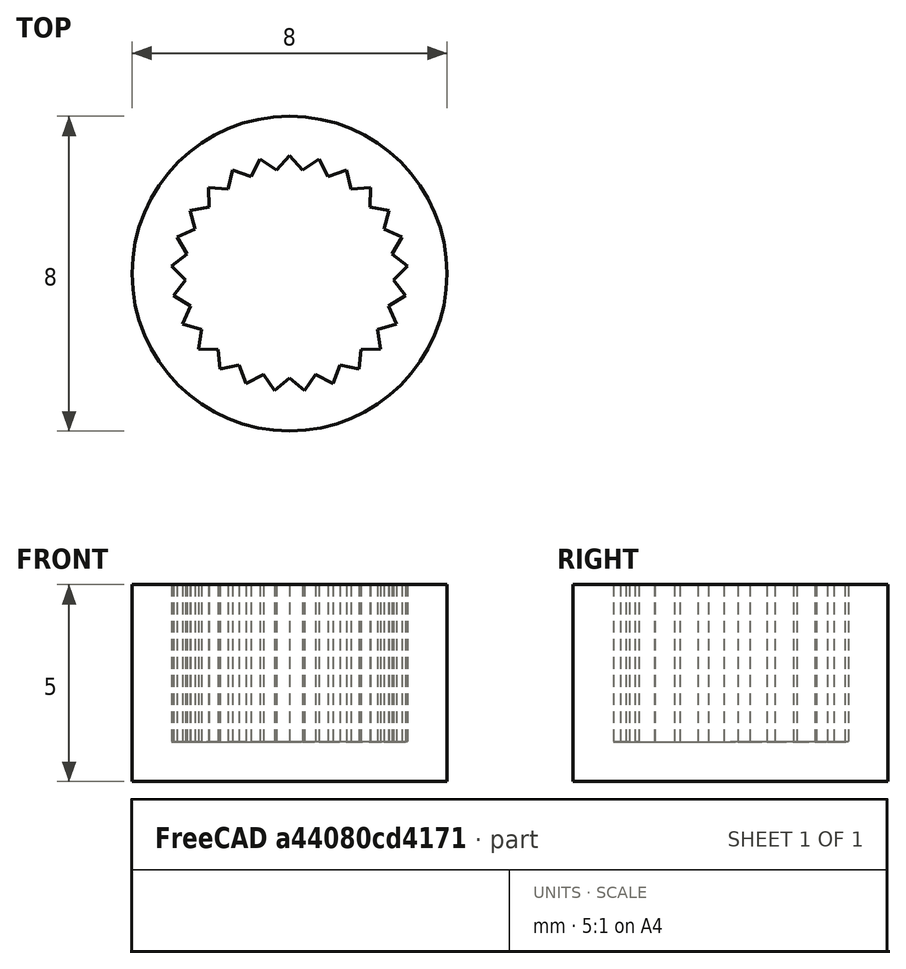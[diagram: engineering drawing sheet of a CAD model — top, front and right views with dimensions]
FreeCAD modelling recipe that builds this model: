
FCSTD DOCUMENT  (FreeCAD 0.20R29410 (Git))
Label: basic_spline
License: All rights reserved
LicenseURL: http://en.wikipedia.org/wiki/All_rights_reserved
objects: Sketcher::SketchObject×2, Mesh::Feature×1, PartDesign::Pad×1, PartDesign::Pocket×1, PartDesign::PolarPattern×1, PartDesign::Body×1
note: 8 computed .brp shape members not serialized (recipe doc carries the construction recipe); baked Part::Feature solids carry a one-line shape summary decoded from their .brp

FEATURE [Mesh::Feature] MG996R
FEATURE [Sketcher::SketchObject] Sketch
  FullyConstrained = true
  MapMode = 5
  Support = -> [XY_Plane]
  sketch-geometry (1):
    g0: Circle CenterX=0 CenterY=0 CenterZ=0 NormalX=0 NormalY=0 NormalZ=1 AngleXU=0 Radius=4
  constraints (2):
    c: Coincident(g0,g-1)
    c: Diameter(g0) = 8
FEATURE [PartDesign::Pad] Pad  label="cylinder_base_Pad"
  Direction = (0,0,1)
  Length = 5
  Length2 = 10
  Profile = -> Sketch
  ReferenceAxis = -> Sketch [N_Axis]
  Type = 0
FEATURE [Sketcher::SketchObject] Sketch001
  FullyConstrained = true
  MapMode = 5
  Placement = pos=(0,0,5) rot=(0,0,1;0rad)
  Support = -> [Pad]
  sketch-geometry (10):
    g0: Circle CenterX=0 CenterY=0 CenterZ=0 NormalX=0 NormalY=0 NormalZ=1 AngleXU=0 Radius=3
    g1: Circle CenterX=0 CenterY=0 CenterZ=0 NormalX=0 NormalY=0 NormalZ=1 AngleXU=0 Radius=2.65
    g2: GeomPoint X=0 Y=3 Z=0
    g3: GeomPoint X=0.74607 Y=2.90575 Z=0
    g4: GeomPoint X=0.332133 Y=2.6291 Z=0
    g5: LineSegment StartX=0 StartY=3 StartZ=0 EndX=0.332133 EndY=2.6291 EndZ=0
    g6: LineSegment StartX=0.332133 StartY=2.6291 StartZ=0 EndX=0.74607 EndY=2.90575 EndZ=0
    g7: LineSegment StartX=0.74607 StartY=2.90575 StartZ=0 EndX=0 EndY=0 EndZ=0
    g8: LineSegment StartX=0.332133 StartY=2.6291 StartZ=0 EndX=0 EndY=0 EndZ=0
    g9: LineSegment StartX=0 StartY=3 StartZ=0 EndX=0 EndY=0 EndZ=0
  constraints (20):
    c: Coincident(g0,g-1)
    c: Diameter(g0) = 6  '5p82_nominal'
    c: Coincident(g1,g0)
    c: Diameter(g1) = 5.3  '5p27nominal'
    c: PointOnObject(g2,g0)
    c: PointOnObject(g3,g0)
    c: PointOnObject(g4,g1)
    c: Coincident(g5,g2)
    c: Coincident(g5,g4)
    c: Coincident(g6,g4)
    c: Coincident(g6,g3)
    c: Coincident(g7,g3)
    c: Coincident(g7,g0)
    c: Angle(g7,g-2) = 0.251327
    c: Coincident(g8,g4)
    c: Coincident(g8,g7)
    c: Angle(g8,g-2) = 0.125664
    c: Coincident(g9,g2)
    c: Coincident(g9,g7)
    c: Vertical(g9)
FEATURE [PartDesign::Pocket] Pocket  label="spline_pocket"
  BaseFeature = -> Pad
  Direction = (0,0,-1)
  Length = 4
  Length2 = 5
  Profile = -> Sketch001
  ReferenceAxis = -> Sketch001 [N_Axis]
  Type = 0
FEATURE [PartDesign::PolarPattern] PolarPattern  label="spline_PolarPattern"
  Angle = 360
  Axis = -> Sketch001 [N_Axis]
  BaseFeature = -> Pocket
  Occurrences = 25
  Originals = -> [Pocket]
FEATURE [PartDesign::Body] Body
  Group = -> [Sketch,Pad,Sketch001,Pocket,PolarPattern]
  Origin = -> Origin
  Tip = -> PolarPattern
